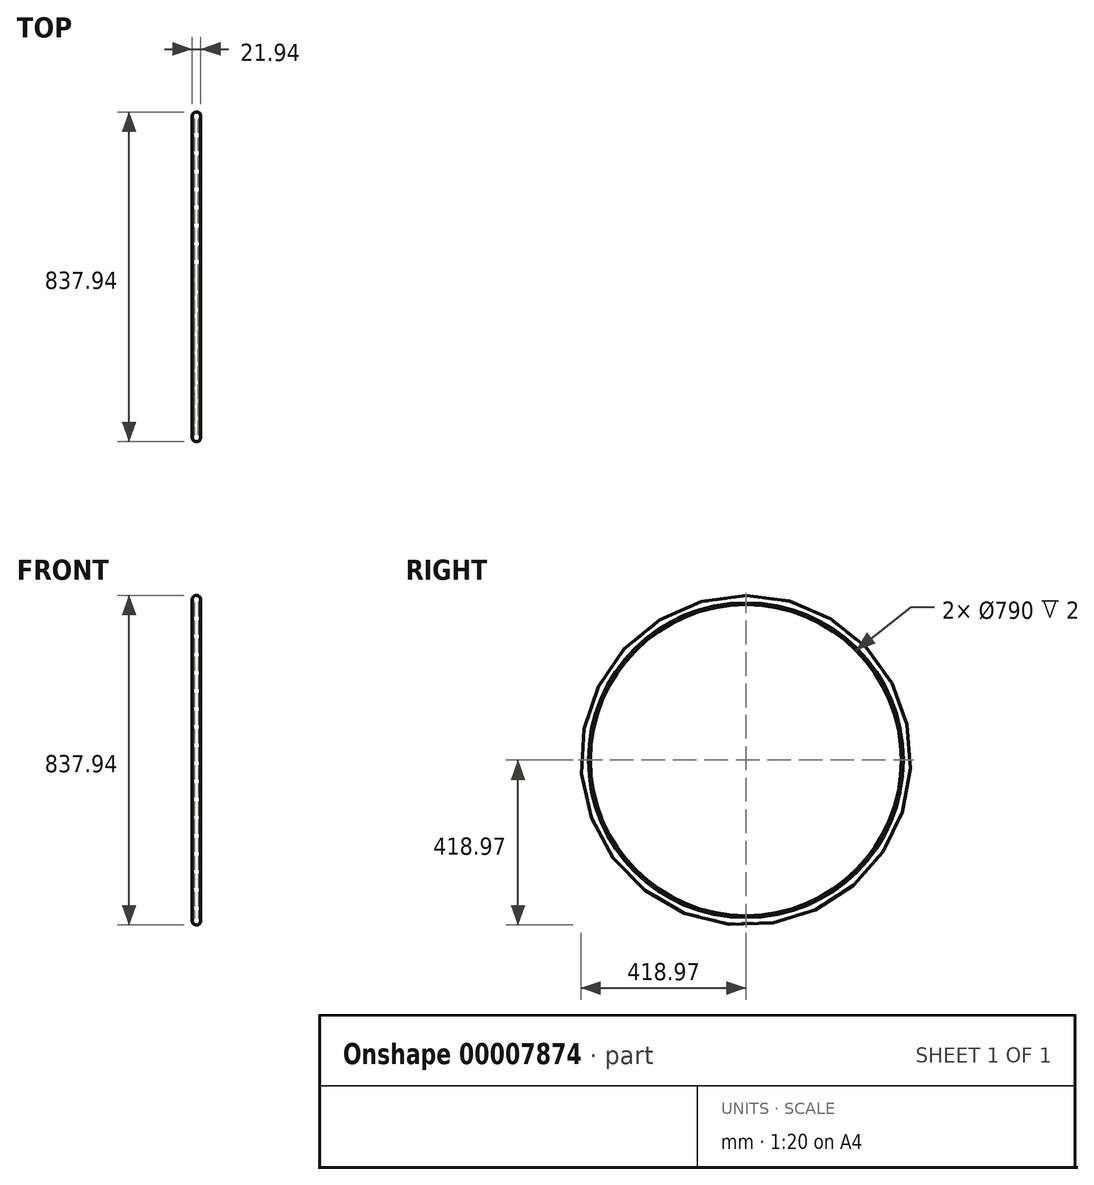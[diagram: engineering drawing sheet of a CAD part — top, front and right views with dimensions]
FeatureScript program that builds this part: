
annotation { "Feature Type Name" : "Feature", "Feature Type Description" : "" }
export const myFeature = defineFeature(function(context is Context, id is Id, definition is map)
    precondition{}
    {
        {
            var Q0;
            Q0=qCreatedBy(makeId("Front.planeOp"),FACE);
            var sketch = newSketch(context, id + "F0", { "sketchPlane" : qUnion([Q0])});
            skLineSegment(sketch, "E0", {"start": v(-101.43, 0) * mm, "end": v(101.43, 0) * mm, "construction": true});
            skLineSegment(sketch, "E1", {"start": v(0, 0) * mm, "end": v(0, 408) * mm, "construction": true});
            skArc(sketch, "E2", {"start": v(-7.5, 400) * mm, "mid": v(0, 397.03) * mm, "end": v(7.5, 400) * mm, "construction": true});
            skArc(sketch, "E3", {"start": v(7.5, 400) * mm, "mid": v(0, 418.97) * mm, "end": v(-7.5, 400) * mm});
            skLineSegment(sketch, "E4", {"start": v(-7.5, 400) * mm, "end": v(7.5, 400) * mm, "construction": true});
            skLineSegment(sketch, "E5", {"start": v(-7.5, 400) * mm, "end": v(-7.5, 395) * mm});
            skLineSegment(sketch, "E6", {"start": v(7.5, 400) * mm, "end": v(7.5, 395) * mm});
            skLineSegment(sketch, "E7.0", {"start": v(-5.5, 400.92) * mm, "end": v(-5.5, 395) * mm});
            skArc(sketch, "E7.1", {"start": v(5.5, 400.92) * mm, "mid": v(0, 416.97) * mm, "end": v(-5.5, 400.92) * mm});
            skLineSegment(sketch, "E7.2", {"start": v(5.5, 400.92) * mm, "end": v(5.5, 395) * mm});
            skLineSegment(sketch, "E8", {"start": v(-7.5, 395) * mm, "end": v(-5.5, 395) * mm});
            skLineSegment(sketch, "E9", {"start": v(5.5, 395) * mm, "end": v(7.5, 395) * mm});
            skSolve(sketch);
        }
        {
            var Q0;
            Q0 = qSketchRegion(id + "F0", true);
            var Q1;
            Q1=sQuery(id+"F0.wireOp",EDGE,"E0");
            revolve(context, id + "F1", {"entities" : qUnion([Q0]), "axis" : qUnion([Q1]), "revolveType" : RevolveType.FULL});
        }
    });
